# Revit family: Hager-Univers-IP44-D205-H800-Cl.II-Encl-PT-pt
name_source: partatom
category: Equipement électrique
units: mm (PartAtom-declared; Revit-internal decimal feet)

## family parameters
Configuration du panneau = Deux colonnes, circuits au sein
Cote de connecteur circulaire = Utiliser le diamètre
Couper avec des vides une fois chargée = Non
Hôte = Face
Partagée = Non
Point de calcul de pièce = Non
Type d'élément = Tableau de raccordement

## types (5) — shared parameters
Commentaires du type = Univers
EF000003 - Método de montagem = EV000384 - Montagem em superfície (gesso)
EF000007 - Cor = EV000202 - Branco
EF000040 - Altura = 800 mm  [stored 2.62467 ft]
EF000049 - Profundidade = 205 mm  [stored 0.672572 ft]
EF000116 - Número RAL = 9010
EF000118 - Com tampa de montagem = Non
EF000218 - Profundidade incorporada = 205 mm  [stored 0.672572 ft]
EF000266 - Número de linhas = 5
EF001088 - Extensão possível = Oui
EF001131 - Profundidade interior = 130 mm  [stored 0.426509 ft]
EF001596 - Material do corpo = EV000179 - Aço
EF001613 - Integridade do circuito = EV000494 - Nenhum
EF003532 - Adequado para uso no exterior = Non
EF004293 - Força de impacto = EV006815 - IK09
EF005474 - Grau de proteção (IP) = EV006418 - IP44
EF006244 - Tampa/porta transparente = Non
EF006306 - Com fecho = Non
EF007800 - Adequado para proteção contra raios = Non
EF008873 - Corrente nominal (In) = 250 A
EF009170 - Espessura do material do invólucro = 1 mm  [stored 0.00328084 ft]
EF009171 - Espessura do material da porta/tampa = 1 mm  [stored 0.00328084 ft]
EF009212 - Tipo de tampa = EV000116 - Fechado
EF015940 - Tampa com libertação de sobrepressão = Non
Fabricant = Hager
HG000002 - Com porta ou tampa = Oui
HG000003 - Gama = Univers
HG000006 - Encastrado = Non
HG000023 - Recinto de secção dupla = Non
HG000024 - Altura da secção inferior = 800 mm  [stored 2.62467 ft]
HG000026 - Instalação no chão = Non
zero-valued in all types: Elévation par défaut, HG000027 - Altura da Plinta

## per-type parameters (varying)
| type | EF000008 - Largura | EF000339 - Tipo de difusor | EF000437 - Número de entradas de condutores | EF002950 - Largura em número de módulos | EF004427 - Número de módulos | EF004464 - Tipo de porta | EF009554 - Número de aberturas para placas de flange | HG000004 - Referência do Fabricante | HG000009 - Porta dupla | HG000010 - Portas assimétricas |
| Montagem em superfície (gesso) IP44 L1050 A800 P205  - FP54SN2 | 1050 mm | EV004216 - Porta | 8 | 48 | 240 | EV003602 - Duplo | 8 | FP54SN2 | Oui | Non |
| Montagem em superfície (gesso) IP44 L1300 A800 P205  - FP55SN2 | 1300 mm  [stored 4.26509 ft] | EV004216 - Porta | 10 | 60 | 300 | EV003602 - Duplo | 10 | FP55SN2 | Oui | Oui |
| Montagem em superfície (gesso) IP44 L300 A800 P205  - FP51SN2 | 300 mm | EV001012 - Tampa | 2 | 12 | 60 | EV002646 - Único | 2 | FP51SN2 | Non | Non |
| Montagem em superfície (gesso) IP44 L550 A800 P205  - FP52SN2 | 550 mm | EV001012 - Tampa | 4 | 24 | 120 | EV002646 - Único | 4 | FP52SN2 | Non | Non |
| Montagem em superfície (gesso) IP44 L800 A800 P205  - FP53SN2 | 800 mm  [stored 2.62467 ft] | EV004216 - Porta | 6 | 36 | 180 | EV002646 - Único | 6 | FP53SN2 | Non | Non |

note: [stored X ft] marks values corroborated as IEEE doubles in the binary element streams (Revit-internal decimal feet)

## geometry (parser evidence)
native form markers: Sweep x10
no freeform markers — native parametric forms only
